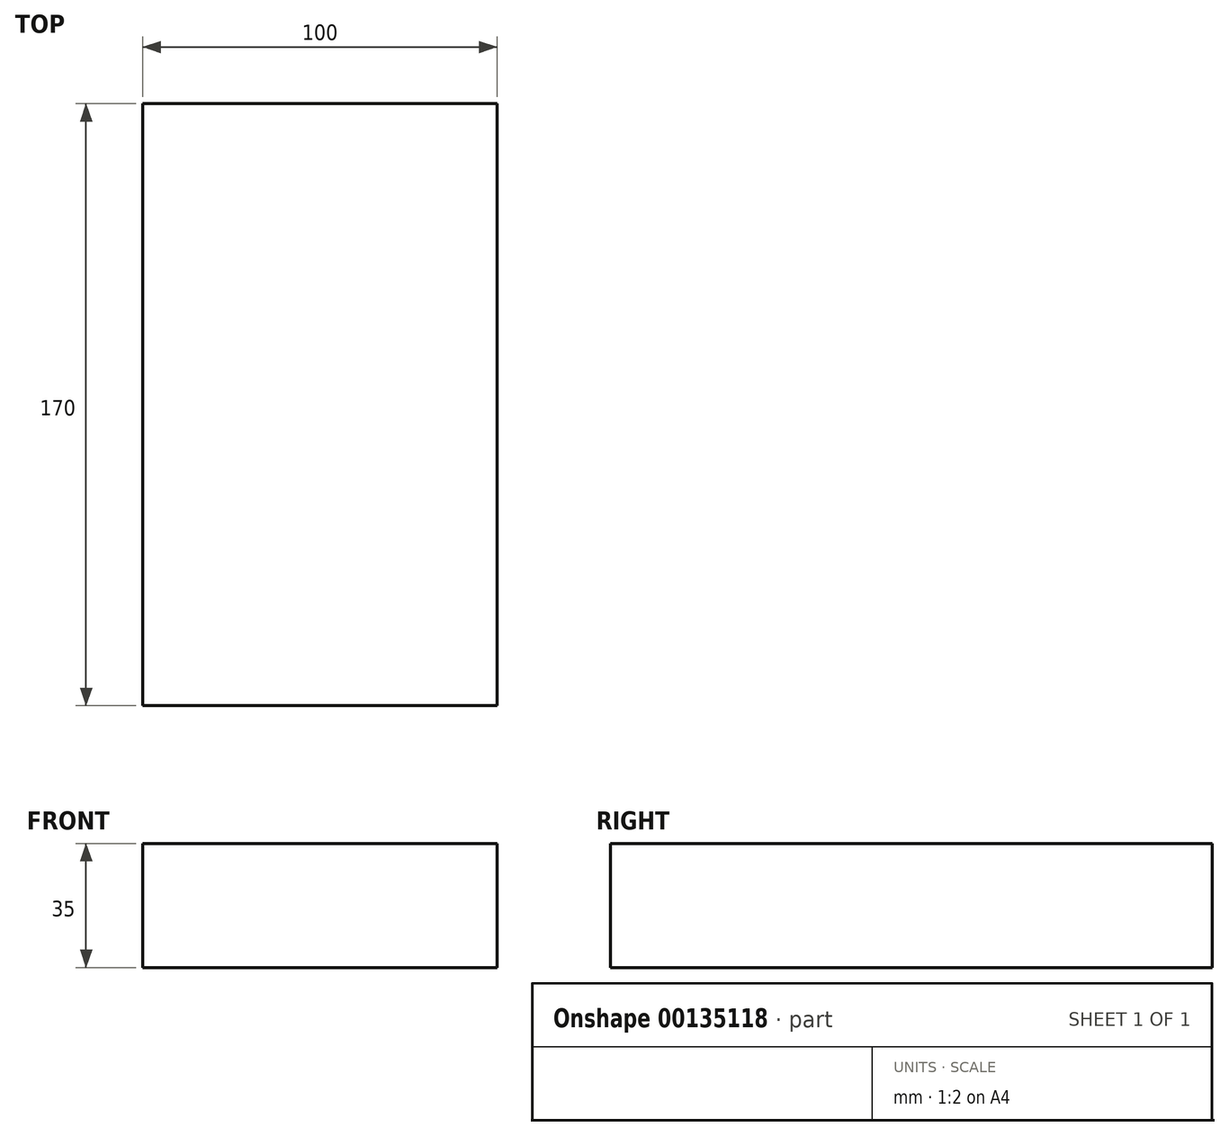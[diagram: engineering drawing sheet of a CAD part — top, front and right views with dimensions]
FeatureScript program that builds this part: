
annotation { "Feature Type Name" : "Feature", "Feature Type Description" : "" }
export const myFeature = defineFeature(function(context is Context, id is Id, definition is map)
    precondition{}
    {
        {
            var Q0;
            Q0=qCreatedBy(makeId("Top.planeOp"),FACE);
            var sketch = newSketch(context, id + "F0", { "sketchPlane" : qUnion([Q0])});
            skLineSegment(sketch, "E0.bottom", {"start": v(-63.42, 150.17) * mm, "end": v(36.58, 150.17) * mm});
            skLineSegment(sketch, "E0.top", {"start": v(-63.42, -19.83) * mm, "end": v(36.58, -19.83) * mm});
            skLineSegment(sketch, "E0.left", {"start": v(-63.42, 150.17) * mm, "end": v(-63.42, -19.83) * mm});
            skLineSegment(sketch, "E0.right", {"start": v(36.58, 150.17) * mm, "end": v(36.58, -19.83) * mm});
            skSolve(sketch);
        }
        {
            var Q0;
            Q0 = qSketchRegion(id + "F0", true);
            extrude(context, id + "F1", {"entities" : qUnion([Q0]), "depth" : 35 * mm});
        }
    });
